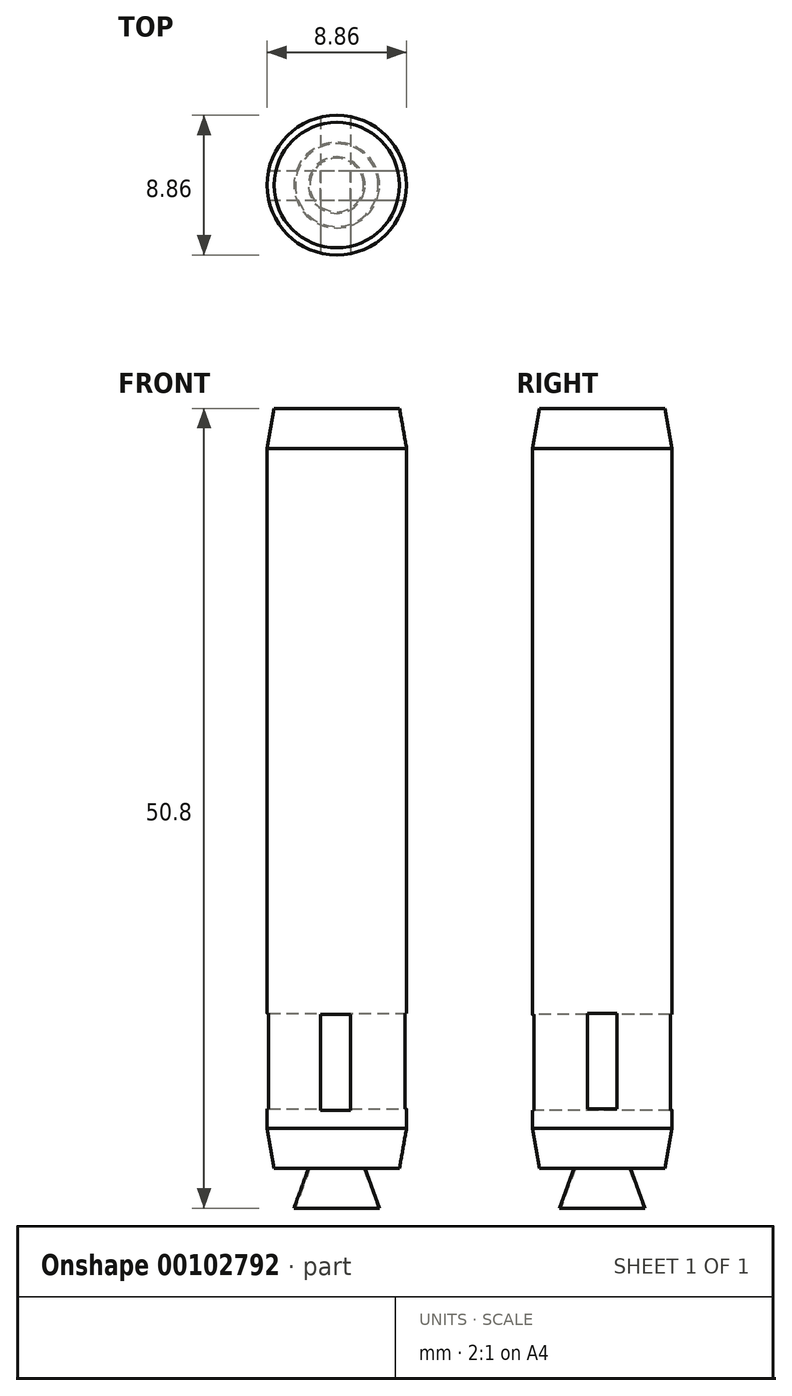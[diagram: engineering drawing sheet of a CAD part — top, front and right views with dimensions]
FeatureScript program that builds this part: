
annotation { "Feature Type Name" : "Feature", "Feature Type Description" : "" }
export const myFeature = defineFeature(function(context is Context, id is Id, definition is map)
    precondition{}
    {
        {
            var Q0;
            Q0=qCreatedBy(makeId("Top.planeOp"),FACE);
            var sketch = newSketch(context, id + "F0", { "sketchPlane" : qUnion([Q0])});
            skCircle(sketch, "E0", {"center": v(0, 0) * mm, "radius": 4.43 * mm});
            skSolve(sketch);
        }
        {
            var Q0;
            Q0=makeQuery(id+"F0.imprint","IMPRINT",FACE,{"disambiguationData":[TD([[makeQuery(id+"F0.imprint","IMPRINT",EDGE,{"derivedFrom":sQuery(id+"F0.wireOp",EDGE,"E0")}),1.0]])]});
            extrude(context, id + "F1", {"entities" : qUnion([Q0]), "depth" : 5.08 * mm, "hasSecondDirection" : true, "secondDirectionOppositeDirection" : true, "secondDirectionDepth" : 38.1 * mm});
        }
        {
            var Q0;
            Q0=makeQuery(id+"F1.opExtrude","CAP_FACE",FACE,{"disambiguationData":[OSD([sQuery(id+"F0.wireOp",EDGE,"E0")])],"isStart":true});
            extrude(context, id + "F2", {"entities" : qUnion([Q0]), "operationType" : NewBodyOperationType.ADD, "depth" : 2.54 * mm, "hasDraft" : true, "draftAngle" : 10 * degree, "draftPullDirection" : true});
        }
        {
            var Q0;
            Q0=makeQuery(id+"F1.opExtrude","CAP_FACE",FACE,{"disambiguationData":[OSD([sQuery(id+"F0.wireOp",EDGE,"E0")])],"isStart":false});
            extrude(context, id + "F3", {"entities" : qUnion([Q0]), "operationType" : NewBodyOperationType.ADD, "depth" : 2.54 * mm, "hasDraft" : true, "draftAngle" : 10 * degree, "draftPullDirection" : true});
        }
        {
            var Q0;
            Q0=makeQuery(id+"F2.opExtrude","CAP_FACE",FACE,{"disambiguationData":[OSD([sQuery(id+"F0.wireOp",EDGE,"E0")])],"isStart":false});
            var sketch = newSketch(context, id + "F4", { "sketchPlane" : qUnion([Q0])});
            skCircle(sketch, "E1", {"center": v(0, 0) * mm, "radius": 1.8 * mm});
            skSolve(sketch);
        }
        {
            var Q0;
            Q0 = qSketchRegion(id + "F4", true);
            extrude(context, id + "F5", {"entities" : qUnion([Q0]), "operationType" : NewBodyOperationType.ADD, "depth" : 2.54 * mm, "hasDraft" : true, "draftAngle" : 20 * degree});
        }
        {
            var Q0;
            Q0=makeQuery(id+"F5.opExtrude","CAP_FACE",FACE,{"disambiguationData":[OSD([sQuery(id+"F4.wireOp",EDGE,"E1")])],"isStart":false});
            var sketch = newSketch(context, id + "F6", { "sketchPlane" : qUnion([Q0])});
            skCircle(sketch, "E2", {"center": v(0, 0) * mm, "radius": 2.63 * mm});
            skSolve(sketch);
        }
        {
            var Q0;
            Q0 = qSketchRegion(id + "F6", true);
            extrude(context, id + "F7", {"entities" : qUnion([Q0]), "operationType" : NewBodyOperationType.REMOVE, "oppositeDirection" : true, "depth" : 2.54 * mm, "hasDraft" : true, "draftAngle" : 20 * degree, "draftPullDirection" : true});
        }
        {
            var Q0;
            Q0=qCreatedBy(makeId("Right.planeOp"),FACE);
            var sketch = newSketch(context, id + "F8", { "sketchPlane" : qUnion([Q0])});
            skLineSegment(sketch, "E3.bottom", {"start": v(-0.95, -30.8) * mm, "end": v(0.93, -30.8) * mm});
            skLineSegment(sketch, "E3.top", {"start": v(-0.95, -36.89) * mm, "end": v(0.93, -36.89) * mm});
            skLineSegment(sketch, "E3.left", {"start": v(-0.95, -30.8) * mm, "end": v(-0.95, -36.89) * mm});
            skLineSegment(sketch, "E3.right", {"start": v(0.93, -30.8) * mm, "end": v(0.93, -36.89) * mm});
            skSolve(sketch);
        }
        {
            var Q0;
            Q0 = qSketchRegion(id + "F8", true);
            extrude(context, id + "F9", {"entities" : qUnion([Q0]), "operationType" : NewBodyOperationType.REMOVE, "oppositeDirection" : true, "depth" : 25.4 * mm, "hasSecondDirection" : true, "secondDirectionOppositeDirection" : false, "secondDirectionDepth" : 25.4 * mm});
        }
        {
            var Q0;
            Q0=qCreatedBy(makeId("Front.planeOp"),FACE);
            var sketch = newSketch(context, id + "F10", { "sketchPlane" : qUnion([Q0])});
            skLineSegment(sketch, "E4.bottom", {"start": v(-1.03, -30.89) * mm, "end": v(0.86, -30.89) * mm});
            skLineSegment(sketch, "E4.top", {"start": v(-1.03, -36.97) * mm, "end": v(0.86, -36.97) * mm});
            skLineSegment(sketch, "E4.left", {"start": v(-1.03, -30.89) * mm, "end": v(-1.03, -36.97) * mm});
            skLineSegment(sketch, "E4.right", {"start": v(0.86, -30.89) * mm, "end": v(0.86, -36.97) * mm});
            skSolve(sketch);
        }
        {
            var Q0;
            Q0 = qSketchRegion(id + "F10", true);
            extrude(context, id + "F11", {"entities" : qUnion([Q0]), "operationType" : NewBodyOperationType.REMOVE, "oppositeDirection" : true, "depth" : 25.4 * mm, "hasSecondDirection" : true, "secondDirectionOppositeDirection" : false, "secondDirectionDepth" : 25.4 * mm});
        }
    });
